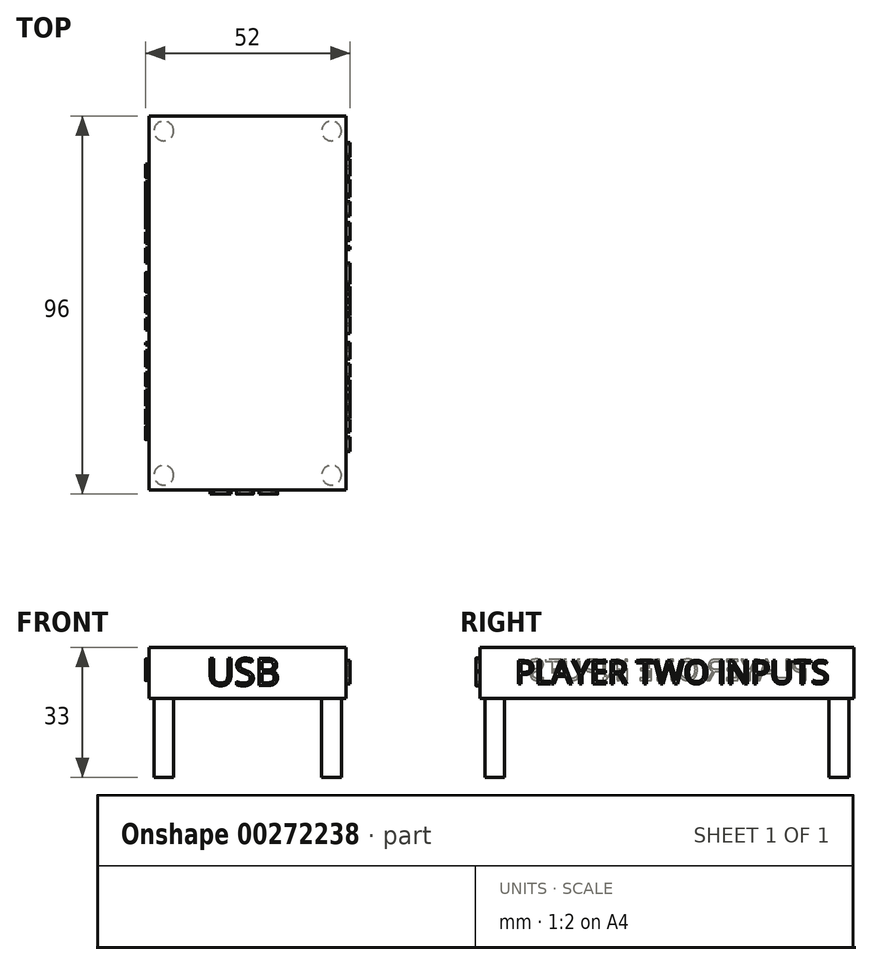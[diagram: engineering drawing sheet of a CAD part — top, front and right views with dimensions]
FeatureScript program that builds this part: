
annotation { "Feature Type Name" : "Feature", "Feature Type Description" : "" }
export const myFeature = defineFeature(function(context is Context, id is Id, definition is map)
    precondition{}
    {
        {
            var Q0;
            Q0=qCreatedBy(makeId("Top.planeOp"),FACE);
            var sketch = newSketch(context, id + "F0", { "sketchPlane" : qUnion([Q0])});
            skLineSegment(sketch, "E0.bottom", {"start": v(25, -47.5) * mm, "end": v(-25, -47.5) * mm});
            skLineSegment(sketch, "E0.top", {"start": v(25, 47.5) * mm, "end": v(-25, 47.5) * mm});
            skLineSegment(sketch, "E0.left", {"start": v(25, -47.5) * mm, "end": v(25, 47.5) * mm});
            skLineSegment(sketch, "E0.right", {"start": v(-25, -47.5) * mm, "end": v(-25, 47.5) * mm});
            skPoint(sketch, "E0.middle", {"position": v(0, 0) * mm});
            skSolve(sketch);
        }
        {
            var Q0;
            Q0 = qSketchRegion(id + "F0", true);
            extrude(context, id + "F1", {"entities" : qUnion([Q0]), "depth" : 13 * mm});
        }
        {
            var Q0;
            Q0=makeQuery(id+"F1.opExtrude","SWEPT_FACE",FACE,{"disambiguationData":[OSD([sQuery(id+"F0.wireOp",EDGE,"E0.bottom")])]});
            var sketch = newSketch(context, id + "F2", { "sketchPlane" : qUnion([Q0])});
            skText(sketch, "E1", { "text": "USB\n", "fontName": "OpenSans-Regular.ttf"});
            const initialGuessF2  = {"E1": [-0.01037, 0.00335, 1, 0, 0.00692]};
            skSetInitialGuess(sketch, initialGuessF2);
            skSolve(sketch);
        }
        {
            var Q0;
            Q0 = qSketchRegion(id + "F2", true);
            extrude(context, id + "F3", {"entities" : qUnion([Q0]), "operationType" : NewBodyOperationType.ADD, "depth" : 1 * mm});
        }
        {
            var Q0;
            Q0=makeQuery(id+"F1.opExtrude","SWEPT_FACE",FACE,{"disambiguationData":[OSD([sQuery(id+"F0.wireOp",EDGE,"E0.right")])]});
            var sketch = newSketch(context, id + "F4", { "sketchPlane" : qUnion([Q0])});
            skText(sketch, "E2", { "text": "PLAYER ONE INPUTS", "fontName": "OpenSans-Regular.ttf"});
            const initialGuessF4  = {"E2": [-0.03603, 0.00468, 1, 0, 0.00535]};
            skSetInitialGuess(sketch, initialGuessF4);
            skSolve(sketch);
        }
        {
            var Q0;
            Q0 = qSketchRegion(id + "F4", true);
            extrude(context, id + "F5", {"entities" : qUnion([Q0]), "operationType" : NewBodyOperationType.ADD, "depth" : 1 * mm});
        }
        {
            var Q0;
            Q0=makeQuery(id+"F1.opExtrude","SWEPT_FACE",FACE,{"disambiguationData":[OSD([sQuery(id+"F0.wireOp",EDGE,"E0.left")])]});
            var sketch = newSketch(context, id + "F6", { "sketchPlane" : qUnion([Q0])});
            skText(sketch, "E3", { "text": "PLAYER TWO INPUTS\n", "fontName": "OpenSans-Regular.ttf"});
            const initialGuessF6  = {"E3": [-0.03852, 0.0038, 1, 0, 0.0059]};
            skSetInitialGuess(sketch, initialGuessF6);
            skSolve(sketch);
        }
        {
            var Q0;
            Q0 = qSketchRegion(id + "F6", true);
            extrude(context, id + "F7", {"entities" : qUnion([Q0]), "operationType" : NewBodyOperationType.ADD, "depth" : 1 * mm});
        }
        {
            var Q0;
            Q0=makeQuery(id+"F1.opExtrude","CAP_FACE",FACE,{"disambiguationData":[OSD([sQuery(id+"F0.wireOp",EDGE,"E0.bottom"),sQuery(id+"F0.wireOp",EDGE,"E0.top"),sQuery(id+"F0.wireOp",EDGE,"E0.left"),sQuery(id+"F0.wireOp",EDGE,"E0.right")])],"isStart":true});
            var sketch = newSketch(context, id + "F8", { "sketchPlane" : qUnion([Q0])});
            skCircle(sketch, "E4", {"center": v(-21.3, 43.73) * mm, "radius": 2.5 * mm});
            skCircle(sketch, "E5.MirrorC", {"center": v(21.3, 43.73) * mm, "radius": 2.5 * mm});
            skCircle(sketch, "E6.MirrorC", {"center": v(21.3, -43.73) * mm, "radius": 2.5 * mm});
            skCircle(sketch, "E7.MirrorC", {"center": v(-21.3, -43.73) * mm, "radius": 2.5 * mm});
            skSolve(sketch);
        }
        {
            var Q0;
            Q0 = qSketchRegion(id + "F8", true);
            extrude(context, id + "F9", {"entities" : qUnion([Q0]), "operationType" : NewBodyOperationType.ADD, "depth" : 20 * mm});
        }
    });
